# Revit family: IS_Ceraterm100new_A5686_BIM_NL
name_source: partatom
category: Plumbing Fixtures
revit_build: Autodesk Revit MEP 2014 (Build: 20130308_1515(x64)
units: mm (PartAtom-declared; Revit-internal decimal feet)

## types (1)
- A5686AA - IDEALRAIN DOUCHESYST+CT100+M3HANDD+200MM
    Accessories = www.idealstandardnederland.nl
    AreaUnits = millimeters
    Assembly Code = C1030200
    AssetType = Vast
    BIMObjectName = ISI_IdealStandard_ShowerFittingsPackage_A5686AA
    BREEAMApproved = No
    BarCode = 4015413314640
    Brand = Ideal Standard
    CWFU = 0
    Color = Chroom
    ConnectionType = Sanitair
    Cost = 0 $
    Default Elevation = 1000 mm  [stored 3.28084 ft]
    Description = Idealrain douchesysteem met CeraTherm 100 new douchethermostaat (A955590AA). Ø200 mm hoofddouche van metaal en Ø100 mm handdouche (3 functies). Anti-kalk functie. Watervoerende douchestang met drukknop bediende draaibare en schuifbare houder. Doucheslang "Idealflex" 1750 mm. Aansluiting G1/2" geïntegreerd. CW-3.
    DurationUnit = jaar
    ECA = No
    ExpectedLife = 25
    FaucetFunction = Thermostaatkraan
    FaucetOperation = Tweegreeps
    FaucetType = Douchethermostaat
    Features = Douchesysteem met douchethermostaat (A955590AA). Ø200 mm hoofddouche van metaal en Ø100 mm handdouche (3 functies). Anti-kalk functie. Watervoerende douchestang met drukknop bediende draaibare en schuifbare houder. Doucheslang "Idealflex" 1750 mm. Aansluiting G1/2" geïntegreerd. CW-3.
    Finish = Chroom
    HWFU = 0
    IfcExportAs = IfcSanitaryTerminalType
    IfcExportType = SHOWER
    InstallationInstructions = http://www.idealstandardnederland.nl
    LinearUnits = millimeters
    ManufacturerURL = www.idealstandardnederland.nl
    Material = Messing
    Model = A5686AA
    ModelNumber = A5686AA
    ModelReference = Idealrain douchesysteem met CeraTherm 100 new douchethermostaat (A955590AA). Ø200 mm hoofddouche van metaal en Ø100 mm handdouche (3 functies). Anti-kalk functie. Watervoerende douchestang met drukknop bediende draaibare en schuifbare houder. Doucheslang "Idealflex" 1750 mm. Aansluiting G1/2" geïntegreerd. CW-3.
    NBSDescription = Shower fittings package
    NBSReference = 45-35-70/330
    Name = ShowerFittingsPackage_A5686AA_IdealStandard
    NettWeight = 6.47 kg
    NominalHeight = 90 mm  [stored 0.295276 ft]
    NominalLength = 1008 mm  [stored 3.30709 ft]
    NominalWidth = 320 mm  [stored 1.04987 ft]
    ProductInformation = http://www.idealstandardnederland.nl
    Shape = Gesculptuurd
    Size = 320x1008x90mm
    Space = Internal
    SpareParts = www.idealstandardnederland.nl
    TMV3 = No
    TestPressure = 10 Bar
    URL = www.idealstandardnederland.nl
    Uniclass2 = Pr_40_20_87_75
    Uniclass2015Description = Shower fittings package
    Uniclass2015Reference = Pr_40_20_87_75
    Uniclass2015Version = Products v1.1
    ValveMechanism = Keramische schijven
    ValveOperation = Tweegreeps
    Version = 1
    VolumeUnits = liter
    WFU = 0
    WRAS = No
    WarrantyDescription = Fabrieksgarantie
    WarrantyDurationParts = 5
    WarrantyDurationUnit = jaar
    WaterEfficientProduct = No
    WorkingPressure = 1-5 bar

note: [stored X ft] marks values corroborated as IEEE doubles in the binary element streams (Revit-internal decimal feet)

## geometry (parser evidence)
native form markers: Sweep x1
no freeform markers — native parametric forms only
